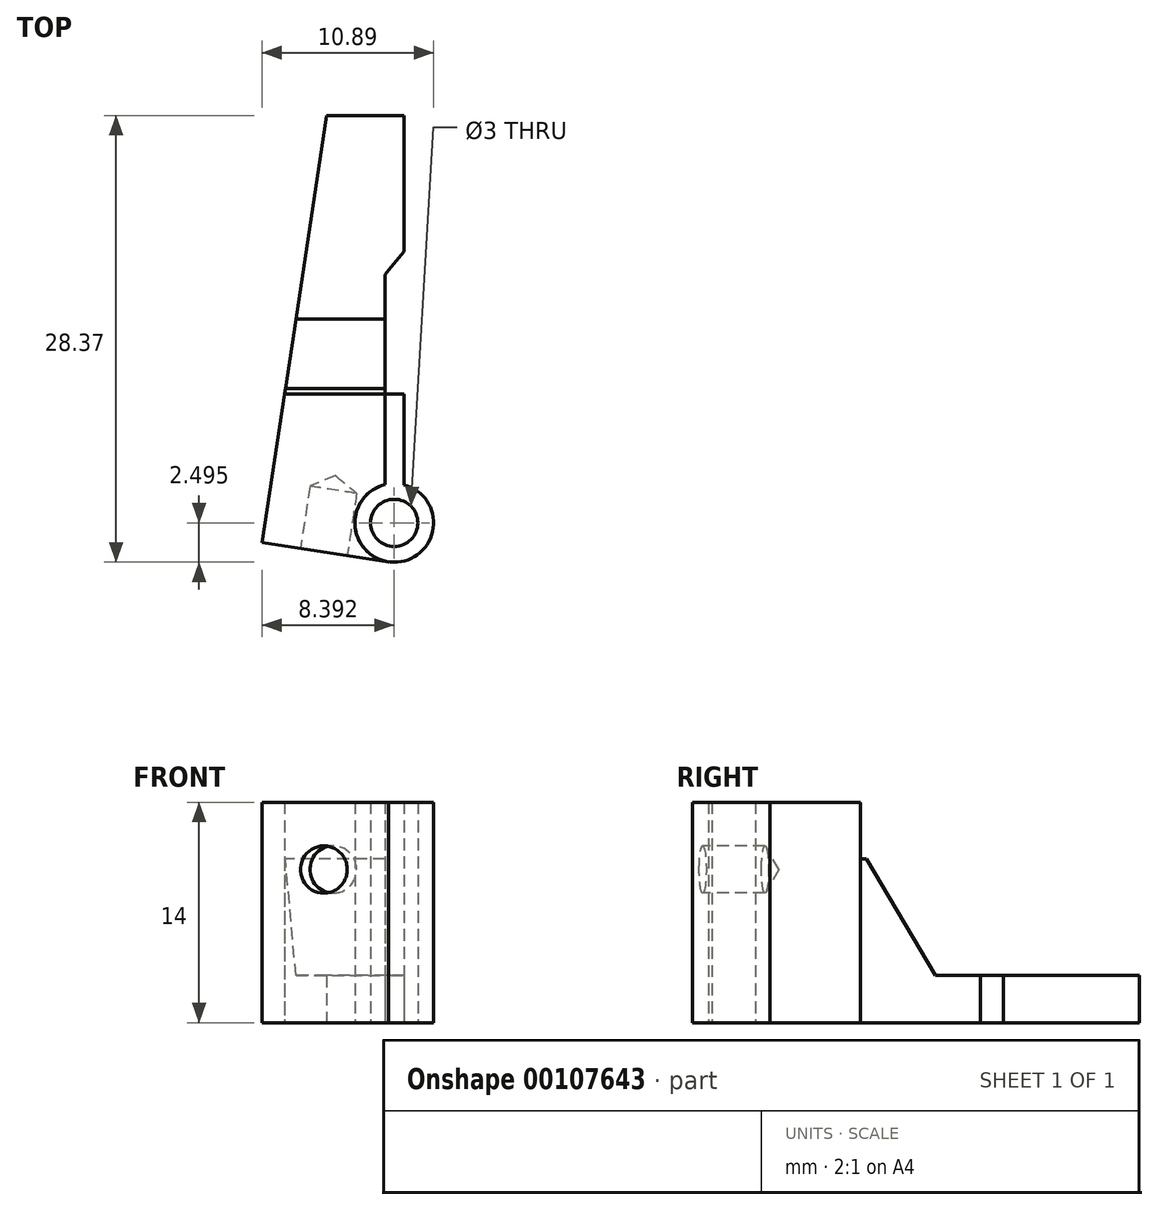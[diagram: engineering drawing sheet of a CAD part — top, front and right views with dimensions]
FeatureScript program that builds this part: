
annotation { "Feature Type Name" : "Feature", "Feature Type Description" : "" }
export const myFeature = defineFeature(function(context is Context, id is Id, definition is map)
    precondition{}
    {
        {
            var Q0;
            Q0=qCreatedBy(makeId("Top.planeOp"),FACE);
            var sketch = newSketch(context, id + "F0", { "sketchPlane" : qUnion([Q0])});
            skCircle(sketch, "E0", {"center": v(-16.65, -12.93) * mm, "radius": 1.5 * mm});
            skLineSegment(sketch, "E1", {"start": v(-16.01, -4.75) * mm, "end": v(-16.01, -10.52) * mm});
            skLineSegment(sketch, "E2", {"start": v(-17.23, -4.75) * mm, "end": v(-23.61, -4.75) * mm});
            skCircle(sketch, "E3", {"center": v(-16.65, -12.93) * mm, "radius": 2.5 * mm});
            skLineSegment(sketch, "E4", {"start": v(-17.02, -15.4) * mm, "end": v(-25.04, -14.2) * mm});
            skLineSegment(sketch, "E5", {"start": v(-16.01, 4.31) * mm, "end": v(-16.01, 12.94) * mm});
            skLineSegment(sketch, "E6", {"start": v(-16.85, 3.3) * mm, "end": v(-16.01, 4.31) * mm});
            skLineSegment(sketch, "E7", {"start": v(-16.01, 12.94) * mm, "end": v(-19.22, 12.94) * mm});
            skLineSegment(sketch, "E8", {"start": v(-19.22, 12.94) * mm, "end": v(-20.93, 12.94) * mm});
            skLineSegment(sketch, "E9", {"start": v(-20.93, 12.94) * mm, "end": v(-25.04, -14.2) * mm});
            skLineSegment(sketch, "E10", {"start": v(-17.23, -4.75) * mm, "end": v(-17.23, 2.84) * mm});
            skLineSegment(sketch, "E11", {"start": v(-16.85, 3.3) * mm, "end": v(-17.23, 2.84) * mm});
            skLineSegment(sketch, "E12", {"start": v(-17.23, -4.75) * mm, "end": v(-17.23, -10.5) * mm});
            skLineSegment(sketch, "E13", {"start": v(-22.9, 0) * mm, "end": v(-17.23, 0) * mm});
            skLineSegment(sketch, "E14", {"start": v(-16.01, -4.75) * mm, "end": v(-17.23, -4.75) * mm});
            skSolve(sketch);
        }
        {
            var Q0;
            Q0=makeQuery(id+"F0.imprint","IMPRINT",FACE,{"disambiguationData":[TD([[makeQuery(id+"F0.imprint","IMPRINT",EDGE,{"derivedFrom":sQuery(id+"F0.wireOp",EDGE,"E0")}),-1.0]])]});
            var Q1;
            {var subQ1=sQuery(id+"F0.wireOp",EDGE,"E1");Q1=makeQuery(id+"F0.imprint","IMPRINT",FACE,{"disambiguationData":[TD([[makeQuery(id+"F0.imprint","IMPRINT",EDGE,{"derivedFrom":subQ1}),-1.0]])]});}
            extrude(context, id + "F1", {"entities" : qUnion([Q0, Q1]), "depth" : 14 * mm});
        }
        {
            var Q0;
            {var subQ3=sQuery(id+"F0.wireOp",EDGE,"E4");Q0=makeQuery(id+"F0.imprint","IMPRINT",FACE,{"disambiguationData":[TD([[makeQuery(id+"F0.imprint","IMPRINT",EDGE,{"derivedFrom":subQ3}),-1.0]])]});}
            extrude(context, id + "F2", {"entities" : qUnion([Q0]), "depth" : 14 * mm});
        }
        {
            var Q0;
            {var subQ5=sQuery(id+"F0.wireOp",EDGE,"E13");Q0=makeQuery(id+"F0.imprint","IMPRINT",FACE,{"disambiguationData":[TD([[makeQuery(id+"F0.imprint","IMPRINT",EDGE,{"derivedFrom":subQ5}),-1.0]])]});}
            extrude(context, id + "F3", {"entities" : qUnion([Q0]), "depth" : 10.4 * mm});
        }
        {
            var Q0;
            Q0=makeQuery(id+"F0.imprint","IMPRINT",FACE,{"disambiguationData":[TD([[makeQuery(id+"F0.imprint","IMPRINT",EDGE,{"derivedFrom":sQuery(id+"F0.wireOp",EDGE,"E5")}),1.0]])]});
            extrude(context, id + "F4", {"entities" : qUnion([Q0]), "operationType" : NewBodyOperationType.ADD, "depth" : 3 * mm});
        }
        {
            var Q0;
            Q0=makeQuery(id+"F3.opExtrude","CAP_EDGE",EDGE,{"disambiguationData":[OSD([sQuery(id+"F0.wireOp",EDGE,"E13")])],"isStart":false});
            chamfer(context, id + "F5", {"entities" : qUnion([Q0]), "chamferType" : ChamferType.TWO_OFFSETS, "width1" : 7.4 * mm, "oppositeDirection" : false, "width2" : 4.4 * mm, "tangentPropagation" : true});
        }
        {
            var Q0;
            Q0=makeQuery(id+"F2.opExtrude","SWEPT_FACE",FACE,{"disambiguationData":[OSD([sQuery(id+"F0.wireOp",EDGE,"E4")])]});
            var sketch = newSketch(context, id + "F6", { "sketchPlane" : qUnion([Q0])});
            skPoint(sketch, "E15", {"position": v(-18.66, 9.73) * mm});
            skSolve(sketch);
        }
        {
            var Q0;
            Q0=sQuery(id+"F6.wireOp",VERTEX,"E15");
            var Q1;
            Q1=makeQuery(id+"F2.opExtrude","SWEPT_BODY",BODY,{"disambiguationData":[OSD([sQuery(id+"F0.wireOp",EDGE,"E2"),sQuery(id+"F0.wireOp",EDGE,"E3"),sQuery(id+"F0.wireOp",EDGE,"E4"),sQuery(id+"F0.wireOp",EDGE,"E9"),sQuery(id+"F0.wireOp",EDGE,"E12")])]});
            hole(context, id + "F7", {"style" : HoleStyle.SIMPLE, "endStyle" : HoleEndStyle.BLIND, "holeDiameter" : 3 * mm, "holeDepth" : 4 * mm, "startFromSketch" : true, "locations" : qUnion([Q0]), "scope" : qUnion([Q1])});
        }
    });
